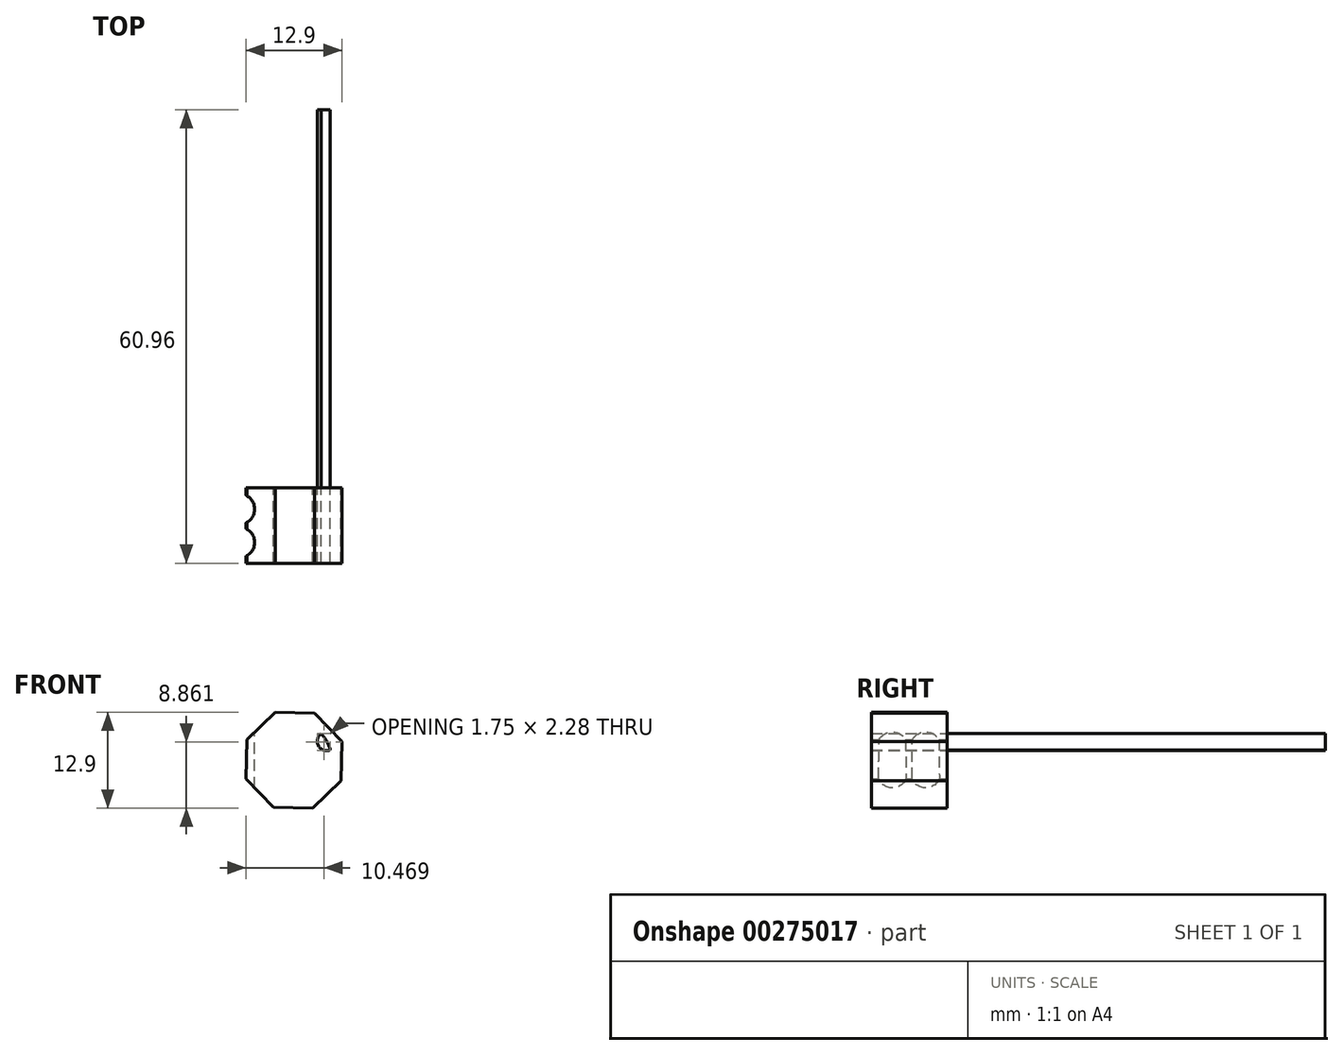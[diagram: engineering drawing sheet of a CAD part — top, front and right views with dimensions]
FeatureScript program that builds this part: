
annotation { "Feature Type Name" : "Feature", "Feature Type Description" : "" }
export const myFeature = defineFeature(function(context is Context, id is Id, definition is map)
    precondition{}
    {
        {
            var Q0;
            Q0=qCreatedBy(makeId("Front.planeOp"),FACE);
            var sketch = newSketch(context, id + "F0", { "sketchPlane" : qUnion([Q0])});
            skCircle(sketch, "E0", {"center": v(0, 0) * mm, "radius": 5.08 * mm});
            skCircle(sketch, "E1", {"center": v(0, 5.08) * mm, "radius": 1.27 * mm});
            skCircle(sketch, "E2.1.0", {"center": v(-4.4, 2.54) * mm, "radius": 1.27 * mm});
            skCircle(sketch, "E2.2.0", {"center": v(-4.4, -2.54) * mm, "radius": 1.27 * mm});
            skCircle(sketch, "E2.3.0", {"center": v(0, -5.08) * mm, "radius": 1.27 * mm});
            skCircle(sketch, "E2.4.0", {"center": v(4.4, -2.54) * mm, "radius": 1.27 * mm});
            skCircle(sketch, "E2.5.0", {"center": v(4.4, 2.54) * mm, "radius": 1.27 * mm});
            skSolve(sketch);
        }
        {
            var Q0;
            {var subQ0=sQuery(id+"F0.wireOp",EDGE,"E2.5.0");var subQ1=sQuery(id+"F0.wireOp",EDGE,"E0");var subQ12=makeQuery(id+"F0.imprint","INTERSECT",VERTEX,{"disambiguationData":[OD(0.0)],"derivedFrom":[subQ1,subQ0]});Q0=makeQuery(id+"F0.imprint","IMPRINT",FACE,{"disambiguationData":[TD([[makeQuery(id+"F0.imprint","IMPRINT",EDGE,{"disambiguationData":[TD([[subQ12,-1.0]])],"derivedFrom":subQ1}),1.0]])]});}
            extrude(context, id + "F1", {"entities" : qUnion([Q0]), "depth" : 50.8 * mm});
        }
        {
            var Q0;
            Q0=makeQuery(id+"F1.opExtrude","CAP_FACE",FACE,{"disambiguationData":[OSD([sQuery(id+"F0.wireOp",EDGE,"E0"),sQuery(id+"F0.wireOp",EDGE,"E1"),sQuery(id+"F0.wireOp",EDGE,"E2.1.0"),sQuery(id+"F0.wireOp",EDGE,"E2.2.0"),sQuery(id+"F0.wireOp",EDGE,"E2.3.0"),sQuery(id+"F0.wireOp",EDGE,"E2.4.0"),sQuery(id+"F0.wireOp",EDGE,"E2.5.0")])],"isStart":false});
            var sketch = newSketch(context, id + "F2", { "sketchPlane" : qUnion([Q0])});
            skCircle(sketch, "E3.cCircle", {"center": v(0, 0) * mm, "radius": 6.4 * mm, "construction": true});
            skLineSegment(sketch, "E3.0", {"start": v(-6.33, 2.79) * mm, "end": v(-2.5, 6.45) * mm});
            skLineSegment(sketch, "E3.1", {"start": v(-2.5, 6.45) * mm, "end": v(2.79, 6.33) * mm});
            skLineSegment(sketch, "E3.2", {"start": v(2.79, 6.33) * mm, "end": v(6.45, 2.5) * mm});
            skLineSegment(sketch, "E3.3", {"start": v(6.45, 2.5) * mm, "end": v(6.33, -2.79) * mm});
            skLineSegment(sketch, "E3.4", {"start": v(6.33, -2.79) * mm, "end": v(2.5, -6.45) * mm});
            skLineSegment(sketch, "E3.5", {"start": v(2.5, -6.45) * mm, "end": v(-2.79, -6.33) * mm});
            skLineSegment(sketch, "E3.6", {"start": v(-2.79, -6.33) * mm, "end": v(-6.45, -2.5) * mm});
            skLineSegment(sketch, "E3.7", {"start": v(-6.45, -2.5) * mm, "end": v(-6.33, 2.79) * mm});
            skPoint(sketch, "E3.0.midPoint", {"position": v(-4.42, 4.62) * mm});
            skSolve(sketch);
        }
        {
            var Q0;
            {var subQ2=sQuery(id+"F0.wireOp",EDGE,"E1");Q0=makeQuery(id+"F2.imprint","IMPRINT",FACE,{"disambiguationData":[TD([[makeQuery(id+"F2.imprint","IMPRINT",EDGE,{"derivedFrom":makeQuery(id+"F1.opExtrude","CAP_EDGE",EDGE,{"disambiguationData":[OSD([subQ2])],"isStart":false})}),-1.0]])]});}
            var Q1;
            Q1=makeQuery(id+"F2.imprint","IMPRINT",FACE,{"disambiguationData":[TD([[makeQuery(id+"F2.imprint","IMPRINT",EDGE,{"derivedFrom":sQuery(id+"F2.wireOp",EDGE,"E3.0")}),-1.0]])]});
            extrude(context, id + "F3", {"entities" : qUnion([Q0, Q1]), "operationType" : NewBodyOperationType.ADD, "depth" : 10.16 * mm});
        }
        {
            var Q0;
            Q0=qCreatedBy(makeId("Top.planeOp"),FACE);
            var sketch = newSketch(context, id + "F4", { "sketchPlane" : qUnion([Q0])});
            skCircle(sketch, "E4", {"center": v(-7.3, -53.68) * mm, "radius": 2.03 * mm});
            skCircle(sketch, "E5", {"center": v(-7.3, -58.15) * mm, "radius": 2.03 * mm});
            skSolve(sketch);
        }
        {
            var Q0;
            Q0=makeQuery(id+"F4.imprint","IMPRINT",FACE,{"disambiguationData":[TD([[makeQuery(id+"F4.imprint","IMPRINT",EDGE,{"derivedFrom":sQuery(id+"F4.wireOp",EDGE,"E4")}),1.0]])]});
            var Q1;
            Q1=makeQuery(id+"F4.imprint","IMPRINT",FACE,{"disambiguationData":[TD([[makeQuery(id+"F4.imprint","IMPRINT",EDGE,{"derivedFrom":sQuery(id+"F4.wireOp",EDGE,"E5")}),1.0]])]});
            extrude(context, id + "F5", {"entities" : qUnion([Q0, Q1]), "operationType" : NewBodyOperationType.REMOVE, "endBound" : BoundingType.SYMMETRIC, "oppositeDirection" : true, "depth" : 25.4 * mm});
        }
    });
